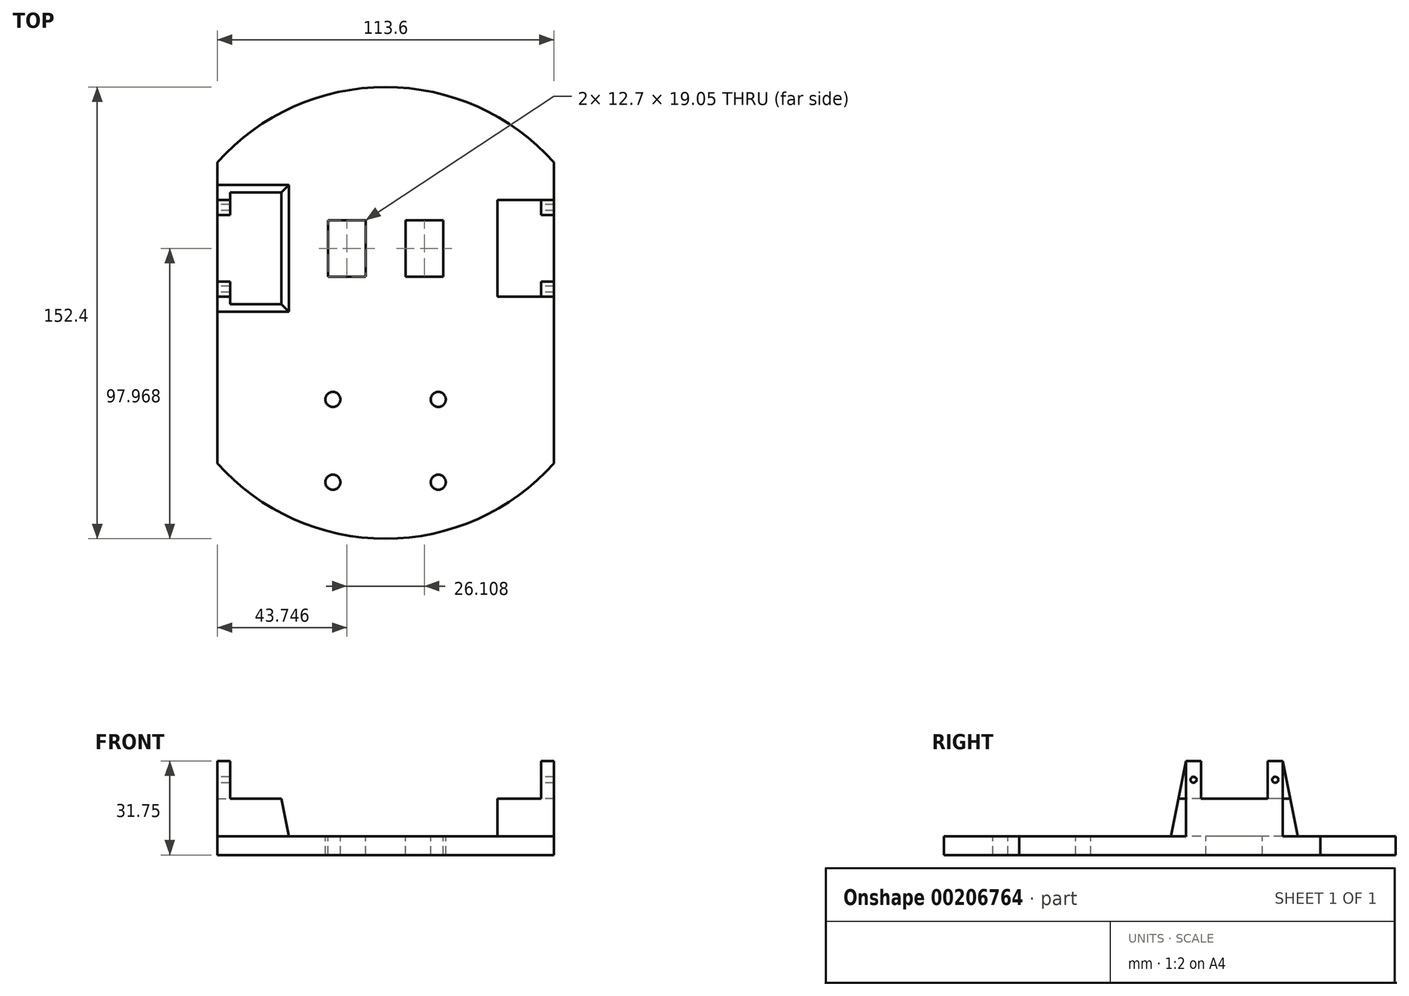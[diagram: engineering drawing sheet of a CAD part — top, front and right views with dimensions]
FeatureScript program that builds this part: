
annotation { "Feature Type Name" : "Feature", "Feature Type Description" : "" }
export const myFeature = defineFeature(function(context is Context, id is Id, definition is map)
    precondition{}
    {
        {
            var Q0;
            Q0=qCreatedBy(makeId("Top.planeOp"),FACE);
            var sketch = newSketch(context, id + "F0", { "sketchPlane" : qUnion([Q0])});
            skArc(sketch, "E0", {"start": v(56.8, 50.8) * mm, "mid": v(0, 76.2) * mm, "end": v(-56.8, 50.8) * mm});
            skLineSegment(sketch, "E1.left", {"start": v(56.8, 50.8) * mm, "end": v(56.8, -50.8) * mm});
            skLineSegment(sketch, "E1.right", {"start": v(-56.8, 50.8) * mm, "end": v(-56.8, -50.8) * mm});
            skArc(sketch, "E2.trimOffspring", {"start": v(-56.8, -50.8) * mm, "mid": v(0, -76.2) * mm, "end": v(56.8, -50.8) * mm});
            skSolve(sketch);
        }
        {
            var Q0;
            Q0=makeQuery(id+"F0.imprint","IMPRINT",FACE,{"disambiguationData":[TD([[makeQuery(id+"F0.imprint","IMPRINT",EDGE,{"derivedFrom":sQuery(id+"F0.wireOp",EDGE,"E0")}),1.0]])]});
            extrude(context, id + "F1", {"entities" : qUnion([Q0]), "depth" : 19.05 * mm});
        }
        {
            var Q0;
            Q0=makeQuery(id+"F1.opExtrude","CAP_FACE",FACE,{"disambiguationData":[OSD([sQuery(id+"F0.wireOp",EDGE,"E0"),sQuery(id+"F0.wireOp",EDGE,"E1.left"),sQuery(id+"F0.wireOp",EDGE,"E1.right"),sQuery(id+"F0.wireOp",EDGE,"E2.trimOffspring")])],"isStart":false});
            var sketch = newSketch(context, id + "F2", { "sketchPlane" : qUnion([Q0])});
            skLineSegment(sketch, "E3.bottom", {"start": v(-56.8, 38.1) * mm, "end": v(-52.48, 38.1) * mm});
            skLineSegment(sketch, "E3.top", {"start": v(-56.8, 33.02) * mm, "end": v(-52.48, 33.02) * mm});
            skLineSegment(sketch, "E3.left", {"start": v(-56.8, 38.1) * mm, "end": v(-56.8, 33.02) * mm});
            skLineSegment(sketch, "E3.right", {"start": v(-52.48, 38.1) * mm, "end": v(-52.48, 33.02) * mm});
            skLineSegment(sketch, "E4.bottom", {"start": v(-56.8, 10.52) * mm, "end": v(-52.48, 10.52) * mm});
            skLineSegment(sketch, "E4.top", {"start": v(-56.8, 5.44) * mm, "end": v(-52.48, 5.44) * mm});
            skLineSegment(sketch, "E4.left", {"start": v(-56.8, 10.52) * mm, "end": v(-56.8, 5.44) * mm});
            skLineSegment(sketch, "E4.right", {"start": v(-52.48, 10.52) * mm, "end": v(-52.48, 5.44) * mm});
            skLineSegment(sketch, "E5", {"start": v(0, 76.2) * mm, "end": v(0, -76.2) * mm, "construction": true});
            skLineSegment(sketch, "E6.MirrorCS", {"start": v(56.8, 10.52) * mm, "end": v(56.8, 5.44) * mm});
            skLineSegment(sketch, "E7.MirrorCS", {"start": v(52.48, 10.52) * mm, "end": v(52.48, 5.44) * mm});
            skLineSegment(sketch, "E8.MirrorCS", {"start": v(56.8, 5.44) * mm, "end": v(52.48, 5.44) * mm});
            skLineSegment(sketch, "E9.MirrorCS", {"start": v(56.8, 10.52) * mm, "end": v(52.48, 10.52) * mm});
            skLineSegment(sketch, "E10.MirrorCS", {"start": v(52.48, 38.1) * mm, "end": v(52.48, 33.02) * mm});
            skLineSegment(sketch, "E11.MirrorCS", {"start": v(56.8, 38.1) * mm, "end": v(56.8, 33.02) * mm});
            skLineSegment(sketch, "E12.MirrorCS", {"start": v(56.8, 33.02) * mm, "end": v(52.48, 33.02) * mm});
            skLineSegment(sketch, "E13.MirrorCS", {"start": v(56.8, 38.1) * mm, "end": v(52.48, 38.1) * mm});
            skSolve(sketch);
        }
        {
            var Q0;
            Q0=makeQuery(id+"F2.imprint","IMPRINT",FACE,{"disambiguationData":[TD([[makeQuery(id+"F2.imprint","IMPRINT",EDGE,{"derivedFrom":sQuery(id+"F2.wireOp",EDGE,"E3.bottom")}),-1.0]])]});
            var Q1;
            Q1=makeQuery(id+"F2.imprint","IMPRINT",FACE,{"disambiguationData":[TD([[makeQuery(id+"F2.imprint","IMPRINT",EDGE,{"derivedFrom":sQuery(id+"F2.wireOp",EDGE,"E4.bottom")}),-1.0]])]});
            var Q2;
            Q2=makeQuery(id+"F2.imprint","IMPRINT",FACE,{"disambiguationData":[TD([[makeQuery(id+"F2.imprint","IMPRINT",EDGE,{"derivedFrom":sQuery(id+"F2.wireOp",EDGE,"E10.MirrorCS")}),1.0]])]});
            var Q3;
            Q3=makeQuery(id+"F2.imprint","IMPRINT",FACE,{"disambiguationData":[TD([[makeQuery(id+"F2.imprint","IMPRINT",EDGE,{"derivedFrom":sQuery(id+"F2.wireOp",EDGE,"E6.MirrorCS")}),-1.0]])]});
            extrude(context, id + "F3", {"entities" : qUnion([Q0, Q1, Q2, Q3]), "operationType" : NewBodyOperationType.ADD, "depth" : 12.7 * mm});
        }
        {
            var Q0;
            Q0=makeQuery(id+"F1.opExtrude","CAP_FACE",FACE,{"disambiguationData":[OSD([sQuery(id+"F0.wireOp",EDGE,"E0"),sQuery(id+"F0.wireOp",EDGE,"E1.left"),sQuery(id+"F0.wireOp",EDGE,"E1.right"),sQuery(id+"F0.wireOp",EDGE,"E2.trimOffspring")])],"isStart":false});
            var sketch = newSketch(context, id + "F4", { "sketchPlane" : qUnion([Q0])});
            skArc(sketch, "E14.0", {"start": v(-56.8, -50.8) * mm, "mid": v(0, -76.2) * mm, "end": v(56.8, -50.8) * mm});
            skArc(sketch, "E15.0", {"start": v(56.8, 50.8) * mm, "mid": v(0, 76.2) * mm, "end": v(-56.8, 50.8) * mm});
            skLineSegment(sketch, "E16", {"start": v(-37.75, 5.44) * mm, "end": v(-37.75, 38.1) * mm});
            skPoint(sketch, "E17.orphan", {"position": v(-56.8, 38.1) * mm});
            skPoint(sketch, "E18.orphan", {"position": v(-56.8, 5.44) * mm});
            skPoint(sketch, "E19.0.end.orphan", {"position": v(56.8, 38.1) * mm});
            skPoint(sketch, "E20.0.start.orphan", {"position": v(56.8, 5.44) * mm});
            skPoint(sketch, "E21.endSnap0", {"position": v(0, -76.2) * mm});
            skLineSegment(sketch, "E22", {"start": v(-37.75, 38.1) * mm, "end": v(-56.8, 38.1) * mm});
            skLineSegment(sketch, "E23", {"start": v(-56.8, 38.1) * mm, "end": v(-56.8, 50.8) * mm});
            skLineSegment(sketch, "E24", {"start": v(-37.75, 5.44) * mm, "end": v(-56.8, 5.44) * mm});
            skLineSegment(sketch, "E25", {"start": v(-56.8, 5.44) * mm, "end": v(-56.8, -50.8) * mm});
            skLineSegment(sketch, "E26", {"start": v(37.75, 38.1) * mm, "end": v(37.75, 5.44) * mm});
            skLineSegment(sketch, "E27", {"start": v(37.75, 5.44) * mm, "end": v(56.8, 5.44) * mm});
            skLineSegment(sketch, "E28", {"start": v(56.8, 5.44) * mm, "end": v(56.8, -50.8) * mm});
            skLineSegment(sketch, "E29", {"start": v(37.75, 38.1) * mm, "end": v(56.8, 38.1) * mm});
            skLineSegment(sketch, "E30", {"start": v(56.8, 38.1) * mm, "end": v(56.8, 50.8) * mm});
            skSolve(sketch);
        }
        {
            var Q0;
            Q0=makeQuery(id+"F4.imprint","IMPRINT",FACE,{"disambiguationData":[TD([[makeQuery(id+"F4.imprint","IMPRINT",EDGE,{"derivedFrom":sQuery(id+"F4.wireOp",EDGE,"E14.0")}),1.0]])]});
            extrude(context, id + "F5", {"entities" : qUnion([Q0]), "operationType" : NewBodyOperationType.REMOVE, "oppositeDirection" : true, "depth" : 12.7 * mm});
        }
        {
            var Q0;
            Q0=makeQuery(id+"F5.boolean.opBoolean","COPY",FACE,{"derivedFrom":makeQuery(id+"F5.opExtrude","CAP_FACE",FACE,{"disambiguationData":[OSD([sQuery(id+"F4.wireOp",EDGE,"E14.0"),sQuery(id+"F4.wireOp",EDGE,"E15.0"),sQuery(id+"F4.wireOp",EDGE,"HLqEBgVw-GmAK-ZShR-xa5N-9hG5Fd1J7bcJ"),sQuery(id+"F4.wireOp",EDGE,"E16"),sQuery(id+"F4.wireOp",EDGE,"K4ycG30X-OxoA-3Jd6-y4d5-MNCXaUvGqbup"),sQuery(id+"F4.wireOp",EDGE,"oCCzcMYt-AbkC-Oil7-1B99-8QIeOJQYWQ4c"),sQuery(id+"F4.wireOp",EDGE,"YYOj1m5M-0dLx-xd19-nRuv-o5vKSCbHdH9f"),sQuery(id+"F4.wireOp",EDGE,"ppC76zu0-NQkY-80CS-Fxpx-rDXYn1zzJWNK"),sQuery(id+"F4.wireOp",EDGE,"M248gyDt-Yucp-qLZ1-goYJ-KHdv2uGrJYS4"),sQuery(id+"F4.wireOp",EDGE,"1YL1kFB1-Jrm3-I8O1-W2ph-EQ6iVHe6pWJg"),sQuery(id+"F4.wireOp",EDGE,"awbl6iUp-pBkk-jTHg-3Si6-pBlneTym22JR"),sQuery(id+"F4.wireOp",EDGE,"iXeKyTrP-0bxX-daeS-unzc-aylYuAXyFVe9")])],"isStart":false})});
            var sketch = newSketch(context, id + "F6", { "sketchPlane" : qUnion([Q0])});
            skLineSegment(sketch, "E31.bottom", {"start": v(17.78, -29.2) * mm, "end": v(-17.78, -29.2) * mm, "construction": true});
            skLineSegment(sketch, "E31.top", {"start": v(17.78, -57.15) * mm, "end": v(-17.78, -57.15) * mm, "construction": true});
            skLineSegment(sketch, "E31.left", {"start": v(17.78, -29.2) * mm, "end": v(17.78, -57.15) * mm, "construction": true});
            skLineSegment(sketch, "E31.right", {"start": v(-17.78, -29.2) * mm, "end": v(-17.78, -57.15) * mm, "construction": true});
            skPoint(sketch, "E31.middle", {"position": v(0, -43.18) * mm});
            skSolve(sketch);
        }
        {
            var Q0;
            Q0=sQuery(id+"F6.wireOp",VERTEX,"E31.bottom.end");
            var Q1;
            Q1=sQuery(id+"F6.wireOp",VERTEX,"E31.bottom.start");
            var Q2;
            Q2=sQuery(id+"F6.wireOp",VERTEX,"E31.top.start");
            var Q3;
            Q3=sQuery(id+"F6.wireOp",VERTEX,"E31.right.end");
            var Q4;
            Q4=makeQuery(id+"F1.opExtrude","SWEPT_BODY",BODY,{"disambiguationData":[OSD([sQuery(id+"F0.wireOp",EDGE,"E0"),sQuery(id+"F0.wireOp",EDGE,"E1.left"),sQuery(id+"F0.wireOp",EDGE,"E1.right"),sQuery(id+"F0.wireOp",EDGE,"E2.trimOffspring")])]});
            hole(context, id + "F7", {"style" : HoleStyle.SIMPLE, "endStyle" : HoleEndStyle.THROUGH, "holeDiameter" : 5.08 * mm, "tappedDepth" : 12.7 * mm, "tapClearance" : 3, "locations" : qUnion([Q0, Q1, Q2, Q3]), "scope" : qUnion([Q4])});
        }
        {
            var Q0;
            Q0=makeQuery(id+"F3.boolean.opBoolean","MERGE",FACE,{"derivedFrom":[makeQuery(id+"F1.opExtrude","SWEPT_FACE",FACE,{"disambiguationData":[OSD([sQuery(id+"F0.wireOp",EDGE,"E1.right")])]}),makeQuery(id+"F3.opExtrude","SWEPT_FACE",FACE,{"disambiguationData":[OSD([sQuery(id+"F2.wireOp",EDGE,"E3.left")])]}),makeQuery(id+"F3.opExtrude","SWEPT_FACE",FACE,{"disambiguationData":[OSD([sQuery(id+"F2.wireOp",EDGE,"E4.left")])]})]});
            var sketch = newSketch(context, id + "F8", { "sketchPlane" : qUnion([Q0])});
            skPoint(sketch, "E32", {"position": v(-35.56, 25.4) * mm});
            skPoint(sketch, "E33", {"position": v(-7.98, 25.4) * mm});
            skSolve(sketch);
        }
        {
            var Q0;
            Q0=sQuery(id+"F8.wireOp",VERTEX,"E32");
            var Q1;
            Q1=sQuery(id+"F8.wireOp",VERTEX,"E33");
            var Q2;
            Q2=makeQuery(id+"F1.opExtrude","SWEPT_BODY",BODY,{"disambiguationData":[OSD([sQuery(id+"F0.wireOp",EDGE,"E0"),sQuery(id+"F0.wireOp",EDGE,"E1.left"),sQuery(id+"F0.wireOp",EDGE,"E1.right"),sQuery(id+"F0.wireOp",EDGE,"E2.trimOffspring")])]});
            hole(context, id + "F9", {"style" : HoleStyle.SIMPLE, "endStyle" : HoleEndStyle.THROUGH, "holeDiameter" : 2.03 * mm, "tappedDepth" : 12.7 * mm, "tapClearance" : 3, "locations" : qUnion([Q0, Q1]), "scope" : qUnion([Q2])});
        }
        {
            var Q0;
            Q0=makeQuery(id+"F1.opExtrude","CAP_FACE",FACE,{"disambiguationData":[OSD([sQuery(id+"F0.wireOp",EDGE,"E0"),sQuery(id+"F0.wireOp",EDGE,"E1.left"),sQuery(id+"F0.wireOp",EDGE,"E1.right"),sQuery(id+"F0.wireOp",EDGE,"E2.trimOffspring")])],"isStart":false});
            var sketch = newSketch(context, id + "F10", { "sketchPlane" : qUnion([Q0])});
            skLineSegment(sketch, "E34", {"start": v(0, 114.39) * mm, "end": v(0, -110.27) * mm, "construction": true});
            skPoint(sketch, "E35", {"position": v(-56.8, 21.77) * mm});
            skPoint(sketch, "E36", {"position": v(56.8, 21.77) * mm});
            skLineSegment(sketch, "E37.bottom", {"start": v(19.4, 31.3) * mm, "end": v(6.7, 31.3) * mm});
            skLineSegment(sketch, "E37.top", {"start": v(19.4, 12.24) * mm, "end": v(6.7, 12.24) * mm});
            skLineSegment(sketch, "E37.left", {"start": v(19.4, 31.3) * mm, "end": v(19.4, 12.24) * mm});
            skLineSegment(sketch, "E37.right", {"start": v(6.7, 31.3) * mm, "end": v(6.7, 12.24) * mm});
            skPoint(sketch, "E37.middle", {"position": v(13.05, 21.77) * mm});
            skLineSegment(sketch, "E38.MirrorCS", {"start": v(-19.4, 12.24) * mm, "end": v(-6.7, 12.24) * mm});
            skLineSegment(sketch, "E39.MirrorCS", {"start": v(-19.4, 31.3) * mm, "end": v(-19.4, 12.24) * mm});
            skPoint(sketch, "E40.MirrorP", {"position": v(-13.05, 21.77) * mm});
            skLineSegment(sketch, "E41.MirrorCS", {"start": v(-19.4, 31.3) * mm, "end": v(-6.7, 31.3) * mm});
            skLineSegment(sketch, "E42.MirrorCS", {"start": v(-6.7, 31.3) * mm, "end": v(-6.7, 12.24) * mm});
            skSolve(sketch);
        }
        {
            var Q0;
            Q0=makeQuery(id+"F10.imprint","IMPRINT",FACE,{"disambiguationData":[TD([[makeQuery(id+"F10.imprint","IMPRINT",EDGE,{"derivedFrom":sQuery(id+"F10.wireOp",EDGE,"E37.bottom")}),1.0]])]});
            var Q1;
            Q1=makeQuery(id+"F10.imprint","IMPRINT",FACE,{"disambiguationData":[TD([[makeQuery(id+"F10.imprint","IMPRINT",EDGE,{"derivedFrom":sQuery(id+"F10.wireOp",EDGE,"E38.MirrorCS")}),1.0]])]});
            extrude(context, id + "F11", {"entities" : qUnion([Q0, Q1]), "operationType" : NewBodyOperationType.REMOVE, "endBound" : BoundingType.THROUGH_ALL, "oppositeDirection" : true, "depth" : 25.4 * mm});
        }
        {
            var Q0;
            Q0=makeQuery(id+"F5.boolean.opBoolean","COPY",EDGE,{"derivedFrom":makeQuery(id+"F5.opExtrude","CAP_EDGE",EDGE,{"disambiguationData":[OSD([sQuery(id+"F4.wireOp",EDGE,"E24")])],"isStart":false})});
            var Q1;
            Q1=makeQuery(id+"F5.boolean.opBoolean","COPY",EDGE,{"derivedFrom":makeQuery(id+"F5.opExtrude","CAP_EDGE",EDGE,{"disambiguationData":[OSD([sQuery(id+"F4.wireOp",EDGE,"E16")])],"isStart":false})});
            var Q2;
            Q2=makeQuery(id+"F5.boolean.opBoolean","COPY",EDGE,{"derivedFrom":makeQuery(id+"F5.opExtrude","CAP_EDGE",EDGE,{"disambiguationData":[OSD([sQuery(id+"F4.wireOp",EDGE,"E22")])],"isStart":false})});
            chamfer(context, id + "F12", {"entities" : qUnion([Q0, Q1, Q2]), "chamferType" : ChamferType.TWO_OFFSETS, "width1" : 5.08 * mm, "oppositeDirection" : false, "width2" : 25.4 * mm, "tangentPropagation" : true});
        }
    });
